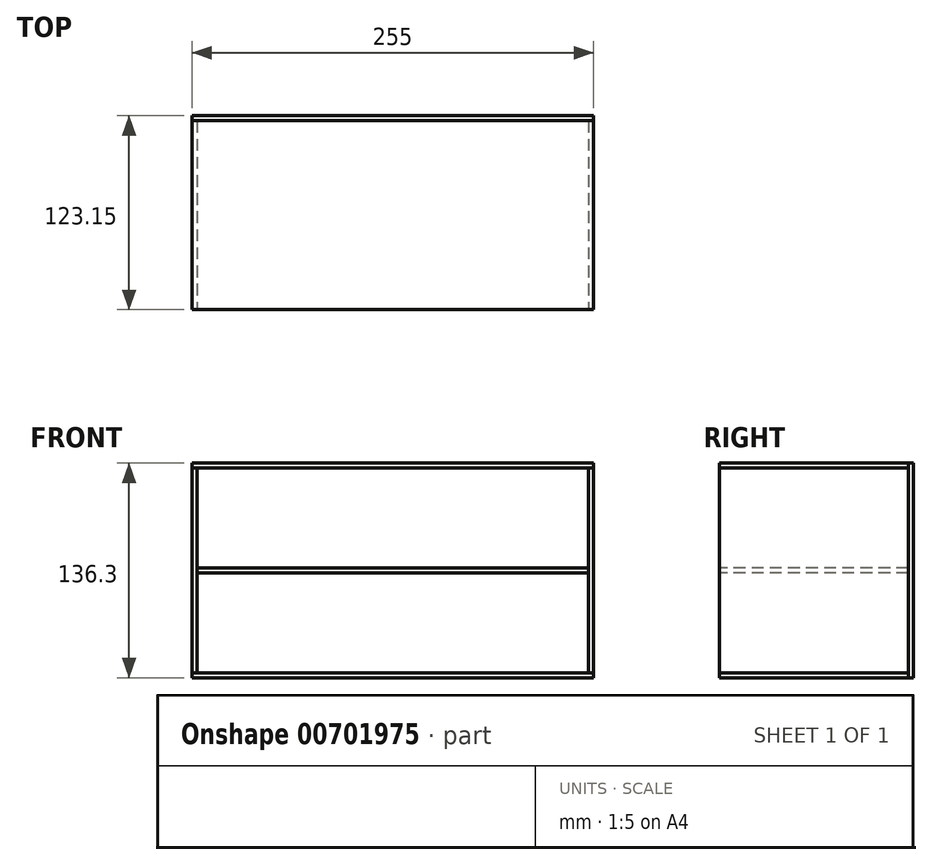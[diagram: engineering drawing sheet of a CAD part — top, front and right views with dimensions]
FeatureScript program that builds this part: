
annotation { "Feature Type Name" : "Feature", "Feature Type Description" : "" }
export const myFeature = defineFeature(function(context is Context, id is Id, definition is map)
    precondition{}
    {
        {
            assignVariable(context, id + "F0", {"name" : "x", "anyValue" : 3.15});
        }
        {
            var Q0;
            Q0=qCreatedBy(makeId("Top.planeOp"),FACE);
            var sketch = newSketch(context, id + "F1", { "sketchPlane" : qUnion([Q0])});
            skLineSegment(sketch, "E0.bottom", {"start": v(0, 0) * mm, "end": v(255, 0) * mm});
            skLineSegment(sketch, "E0.top", {"start": v(0, 120) * mm, "end": v(255, 120) * mm});
            skLineSegment(sketch, "E0.left", {"start": v(0, 0) * mm, "end": v(0, 120) * mm});
            skLineSegment(sketch, "E0.right", {"start": v(255, 0) * mm, "end": v(255, 120) * mm});
            skSolve(sketch);
        }
        {
            var Q0;
            Q0=qSketchRegion(id+"F1",true);
            extrude(context, id + "F2", {"entities" : qUnion([Q0]), "depth" : (getVariable(context, 'x')) * mm, "offsetDistance" : 25 * mm});
        }
        {
            var Q0;
            Q0=makeQuery(id+"F2.opExtrude","SWEPT_FACE",FACE,{"disambiguationData":[OSD([sQuery(id+"F1.wireOp",EDGE,"E0.left")])]});
            var sketch = newSketch(context, id + "F3", { "sketchPlane" : qUnion([Q0])});
            skLineSegment(sketch, "E1.top", {"start": v(0, 133.15) * mm, "end": v(-120, 133.15) * mm});
            skLineSegment(sketch, "E1.left", {"start": v(0, 3.15) * mm, "end": v(0, 133.15) * mm});
            skLineSegment(sketch, "E2", {"start": v(0, 3.15) * mm, "end": v(-120, 3.15) * mm});
            skLineSegment(sketch, "E3", {"start": v(-120, 3.15) * mm, "end": v(-120, 133.15) * mm});
            skSolve(sketch);
        }
        {
            var Q0;
            Q0=qSketchRegion(id+"F3",true);
            extrude(context, id + "F4", {"entities" : qUnion([Q0]), "oppositeDirection" : true, "depth" : (getVariable(context, 'x')) * mm, "offsetDistance" : 25 * mm});
        }
        {
            var Q0;
            Q0=makeQuery(id+"FVTuVMvbx6C6lcW_2.boolean.opBoolean","MERGE",FACE,{"derivedFrom":[makeQuery(id+"F4.opExtrude","SWEPT_FACE",FACE,{"disambiguationData":[OSD([sQuery(id+"F3.wireOp",EDGE,"E1.left")])]}),makeQuery(id+"FVTuVMvbx6C6lcW_2.opExtrude","SWEPT_FACE",FACE,{"disambiguationData":[OSD([sQuery(id+"F9WBSx8lvzqTq6O_2.wireOp",EDGE,"DdJYWYcg-8VXy-0sGO-iMAo-MInbchsGbsPU")])]})]});
            var sketch = newSketch(context, id + "F5", { "sketchPlane" : qUnion([Q0])});
            skLineSegment(sketch, "E4.bottom", {"start": v(3.15, 69.72) * mm, "end": v(251.85, 69.72) * mm});
            skLineSegment(sketch, "E4.top", {"start": v(3.15, 66.57) * mm, "end": v(251.85, 66.57) * mm});
            skLineSegment(sketch, "E4.right", {"start": v(251.85, 69.72) * mm, "end": v(251.85, 66.57) * mm});
            skLineSegment(sketch, "E5", {"start": v(251.85, 3.15) * mm, "end": v(251.85, 66.57) * mm, "construction": true});
            skLineSegment(sketch, "E6", {"start": v(3.15, 66.57) * mm, "end": v(3.15, 69.72) * mm});
            skPoint(sketch, "E7", {"position": v(3.15, 68.15) * mm});
            skSolve(sketch);
        }
        {
            var Q0;
            Q0=qSketchRegion(id+"F5",true);
            var Q1;
            Q1=makeQuery(id+"F4.opExtrude","SWEPT_FACE",FACE,{"disambiguationData":[OSD([sQuery(id+"F3.wireOp",EDGE,"E3")])]});
            extrude(context, id + "F6", {"entities" : qUnion([Q0]), "endBound" : BoundingType.UP_TO_SURFACE, "oppositeDirection" : true, "depth" : 25 * mm, "endBoundEntityFace" : qUnion([Q1]), "offsetDistance" : 25 * mm});
        }
        {
            var Q0;
            Q0=makeQuery(id+"F2.opExtrude","SWEPT_BODY",BODY,{"disambiguationData":[OSD([sQuery(id+"F1.wireOp",EDGE,"E0.bottom"),sQuery(id+"F1.wireOp",EDGE,"E0.top"),sQuery(id+"F1.wireOp",EDGE,"E0.left"),sQuery(id+"F1.wireOp",EDGE,"E0.right")])]});
            transform(context, id + "F7", {"entities" : qUnion([Q0]), "transformType" : TransformType.TRANSLATION_3D, "dx" : 0 * mm, "dy" : 0 * mm, "dz" : 133.15 * mm, "makeCopy" : true});
        }
        {
            var Q0;
            Q0=makeQuery(id+"F4.opExtrude","SWEPT_BODY",BODY,{"disambiguationData":[OSD([sQuery(id+"F3.wireOp",EDGE,"E1.top"),sQuery(id+"F3.wireOp",EDGE,"E1.left"),sQuery(id+"F3.wireOp",EDGE,"E2"),sQuery(id+"F3.wireOp",EDGE,"E3")])]});
            transform(context, id + "F8", {"entities" : qUnion([Q0]), "transformType" : TransformType.TRANSLATION_3D, "dx" : (263.7 + 3.15 - 15) * mm, "dy" : 0 * mm, "dz" : 0 * mm, "makeCopy" : true});
        }
        {
            var Q0;
            Q0=makeQuery(id+"F7.opPattern","COPY",FACE,{"derivedFrom":makeQuery(id+"F2.opExtrude","SWEPT_FACE",FACE,{"disambiguationData":[OSD([sQuery(id+"F1.wireOp",EDGE,"E0.top")])]}),"instanceName":"1"});
            var sketch = newSketch(context, id + "F9", { "sketchPlane" : qUnion([Q0])});
            skLineSegment(sketch, "E8.bottom", {"start": v(-255, 136.3) * mm, "end": v(0, 136.3) * mm});
            skLineSegment(sketch, "E8.top", {"start": v(-255, 0) * mm, "end": v(0, 0) * mm});
            skLineSegment(sketch, "E8.left", {"start": v(-255, 136.3) * mm, "end": v(-255, 0) * mm});
            skLineSegment(sketch, "E8.right", {"start": v(0, 136.3) * mm, "end": v(0, 0) * mm});
            skSolve(sketch);
        }
        {
            var Q0;
            Q0=qSketchRegion(id+"F9",true);
            extrude(context, id + "F10", {"entities" : qUnion([Q0]), "depth" : (getVariable(context, 'x')) * mm, "offsetDistance" : 25 * mm});
        }
    });
